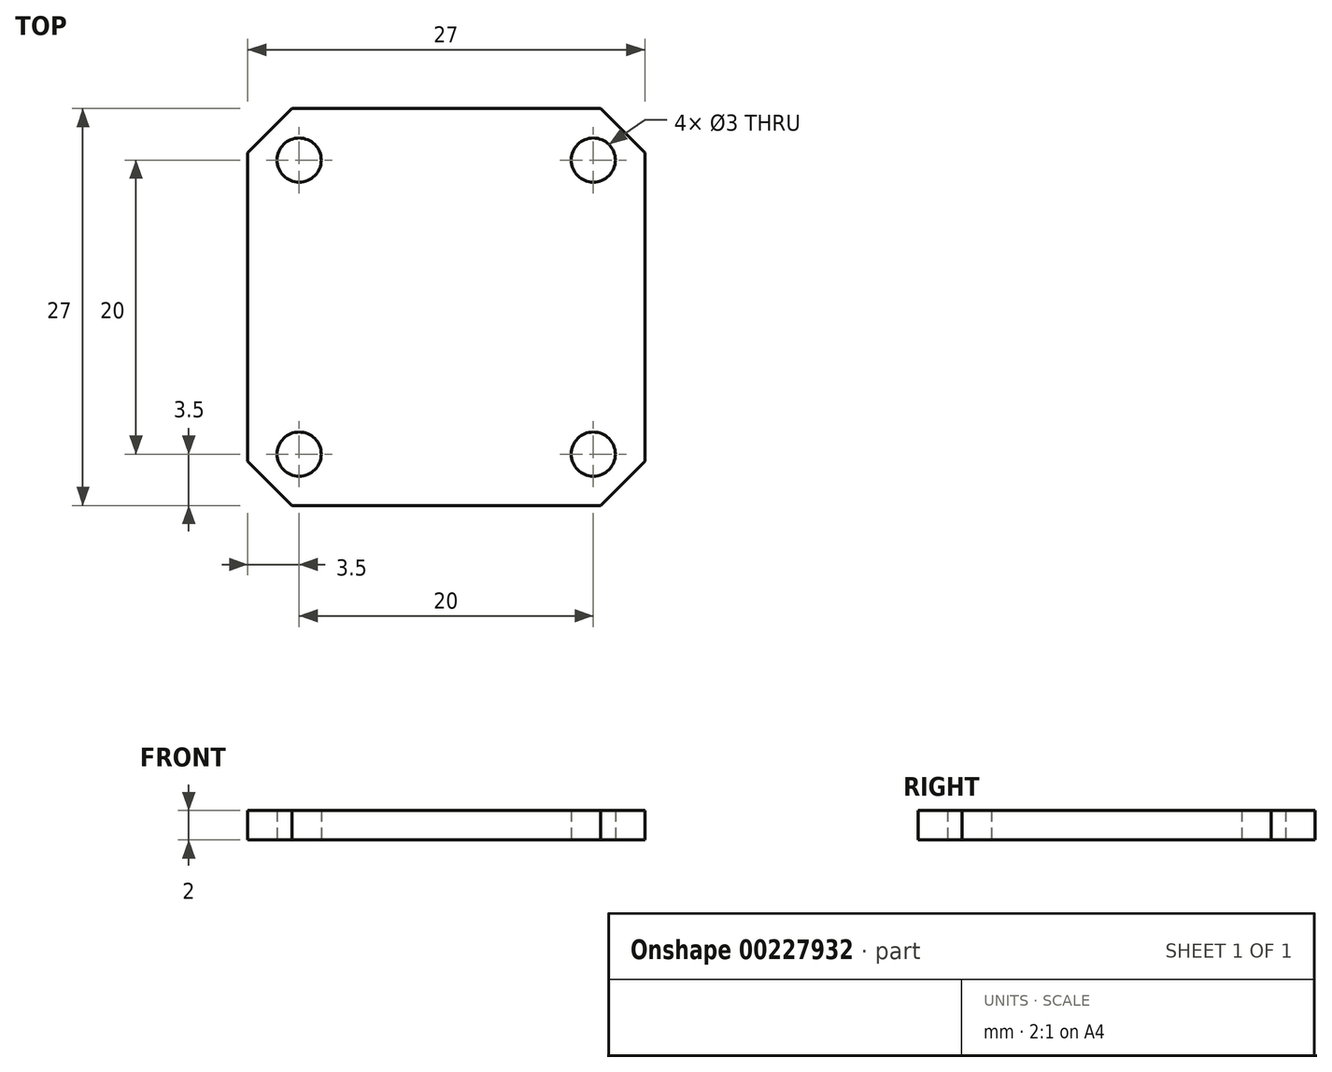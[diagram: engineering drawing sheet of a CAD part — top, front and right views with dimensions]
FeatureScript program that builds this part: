
annotation { "Feature Type Name" : "Feature", "Feature Type Description" : "" }
export const myFeature = defineFeature(function(context is Context, id is Id, definition is map)
    precondition{}
    {
        {
            var Q0;
            Q0=qCreatedBy(makeId("Top.planeOp"),FACE);
            var sketch = newSketch(context, id + "F0", { "sketchPlane" : qUnion([Q0])});
            skLineSegment(sketch, "E0.bottom", {"start": v(-13.5, 13.5) * mm, "end": v(13.5, 13.5) * mm});
            skLineSegment(sketch, "E0.top", {"start": v(-13.5, -13.5) * mm, "end": v(13.5, -13.5) * mm});
            skLineSegment(sketch, "E0.left", {"start": v(-13.5, 13.5) * mm, "end": v(-13.5, -13.5) * mm});
            skLineSegment(sketch, "E0.right", {"start": v(13.5, 13.5) * mm, "end": v(13.5, -13.5) * mm});
            skCircle(sketch, "E1", {"center": v(-10, 10) * mm, "radius": 1.5 * mm});
            skLineSegment(sketch, "E2", {"start": v(-13.5, -13.5) * mm, "end": v(13.5, 13.5) * mm, "construction": true});
            skCircle(sketch, "E3.1.0", {"center": v(-10, -10) * mm, "radius": 1.5 * mm});
            skCircle(sketch, "E3.2.0", {"center": v(10, -10) * mm, "radius": 1.5 * mm});
            skCircle(sketch, "E3.3.0", {"center": v(10, 10) * mm, "radius": 1.5 * mm});
            skPoint(sketch, "E3.center", {"position": v(0, 0) * mm});
            skSolve(sketch);
        }
        {
            var Q0;
            Q0 = qSketchRegion(id + "F0", true);
            extrude(context, id + "F1", {"entities" : qUnion([Q0]), "depth" : 2 * mm});
        }
        {
            var Q0;
            Q0=makeQuery(id+"F1.opExtrude","SWEPT_EDGE",EDGE,{"disambiguationData":[OSD([sQuery(id+"F0.wireOp",EDGE,"E0.top"),sQuery(id+"F0.wireOp",EDGE,"E0.right")])]});
            var Q1;
            Q1=makeQuery(id+"F1.opExtrude","SWEPT_EDGE",EDGE,{"disambiguationData":[OSD([sQuery(id+"F0.wireOp",EDGE,"E0.top"),sQuery(id+"F0.wireOp",EDGE,"E0.left")])]});
            var Q2;
            Q2=makeQuery(id+"F1.opExtrude","SWEPT_EDGE",EDGE,{"disambiguationData":[OSD([sQuery(id+"F0.wireOp",EDGE,"E0.bottom"),sQuery(id+"F0.wireOp",EDGE,"E0.right")])]});
            var Q3;
            Q3=makeQuery(id+"F1.opExtrude","SWEPT_EDGE",EDGE,{"disambiguationData":[OSD([sQuery(id+"F0.wireOp",EDGE,"E0.bottom"),sQuery(id+"F0.wireOp",EDGE,"E0.left")])]});
            chamfer(context, id + "F2", {"entities" : qUnion([Q0, Q1, Q2, Q3]), "width" : 3 * mm, "tangentPropagation" : true});
        }
    });
